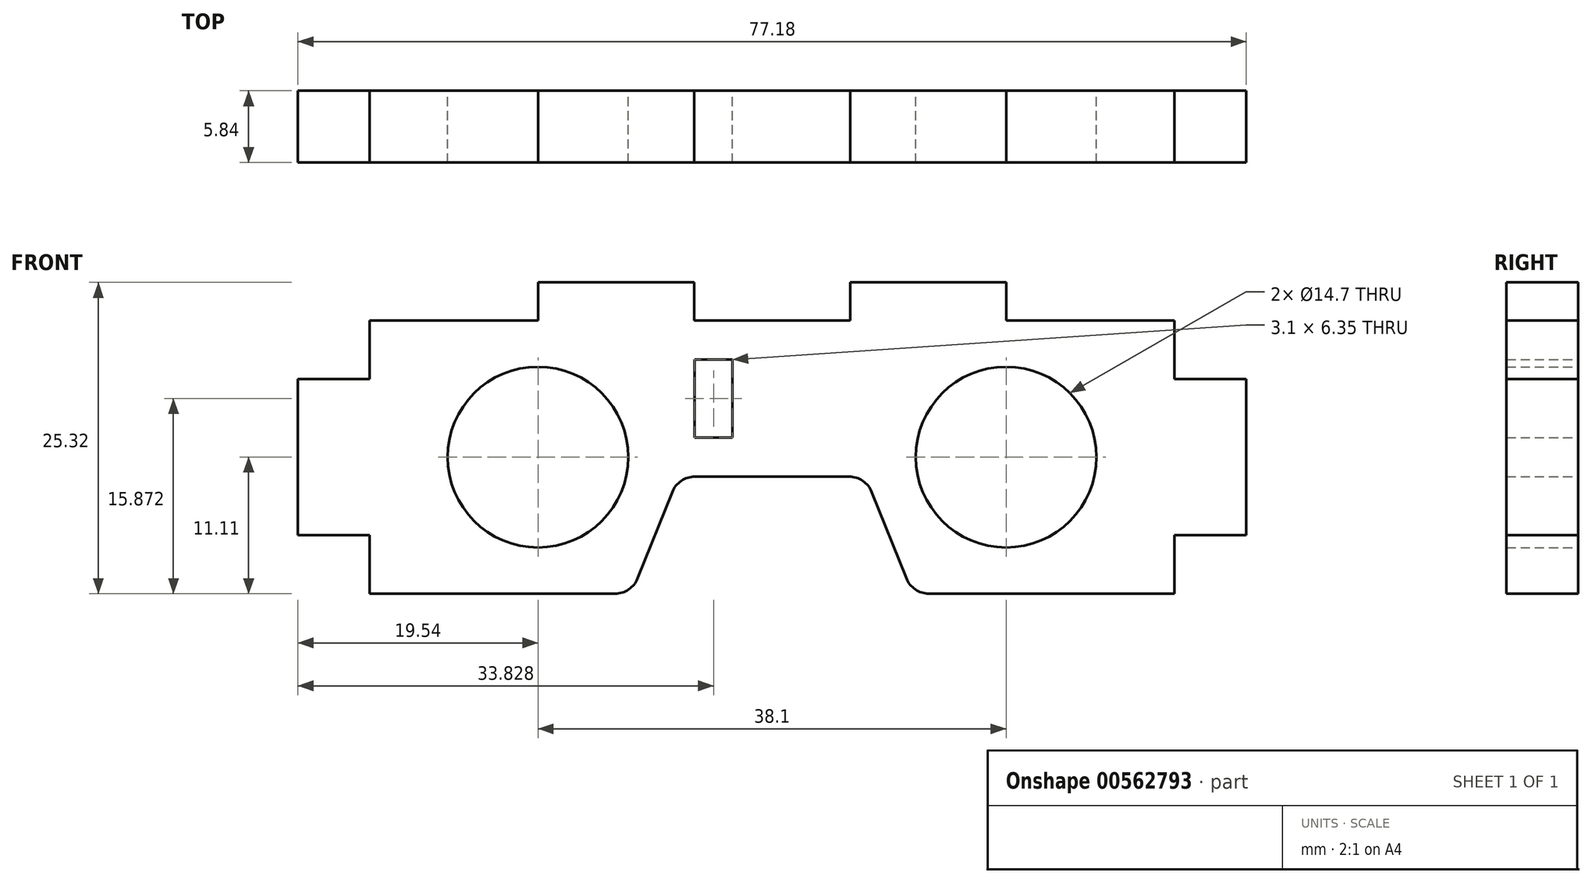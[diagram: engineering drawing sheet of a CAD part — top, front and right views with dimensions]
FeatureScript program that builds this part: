
annotation { "Feature Type Name" : "Feature", "Feature Type Description" : "" }
export const myFeature = defineFeature(function(context is Context, id is Id, definition is map)
    precondition{}
    {
        {
            var Q0;
            Q0=qCreatedBy(makeId("Front.planeOp"),FACE);
            var sketch = newSketch(context, id + "F0", { "sketchPlane" : qUnion([Q0])});
            skCircle(sketch, "E0", {"center": v(-19.05, 0) * mm, "radius": 7.35 * mm});
            skCircle(sketch, "E1.MirrorC", {"center": v(19.05, 0) * mm, "radius": 7.35 * mm});
            skLineSegment(sketch, "E2.bottom", {"start": v(-31.75, 11.11) * mm, "end": v(31.75, 11.11) * mm});
            skLineSegment(sketch, "E2.top", {"start": v(-31.75, -11.11) * mm, "end": v(-11.43, -11.11) * mm});
            skLineSegment(sketch, "E2.left", {"start": v(-31.75, 11.11) * mm, "end": v(-31.75, -11.11) * mm});
            skLineSegment(sketch, "E2.right", {"start": v(31.75, 11.11) * mm, "end": v(31.75, -11.11) * mm});
            skPoint(sketch, "E2.middle", {"position": v(0, 0) * mm});
            skLineSegment(sketch, "E3", {"start": v(-11.43, -11.11) * mm, "end": v(-7.62, -1.59) * mm});
            skLineSegment(sketch, "E4", {"start": v(-7.62, -1.59) * mm, "end": v(0, -1.59) * mm});
            skLineSegment(sketch, "E5.MirrorCS", {"start": v(7.62, -1.59) * mm, "end": v(0, -1.59) * mm});
            skLineSegment(sketch, "E6.MirrorCS", {"start": v(11.43, -11.11) * mm, "end": v(7.62, -1.59) * mm});
            skLineSegment(sketch, "E7.trimOffspring", {"start": v(11.43, -11.11) * mm, "end": v(31.75, -11.11) * mm});
            skSolve(sketch);
        }
        {
            var Q0;
            Q0=makeQuery(id+"F0.imprint","IMPRINT",FACE,{"disambiguationData":[TD([[makeQuery(id+"F0.imprint","IMPRINT",EDGE,{"derivedFrom":sQuery(id+"F0.wireOp",EDGE,"E0")}),-1.0]])]});
            extrude(context, id + "F1", {"entities" : qUnion([Q0]), "depth" : 5.84 * mm, "offsetDistance" : 25.4 * mm});
        }
        {
            var Q0;
            Q0=makeQuery(id+"F1.opExtrude","SWEPT_EDGE",EDGE,{"disambiguationData":[OSD([sQuery(id+"F0.wireOp",EDGE,"E2.top"),sQuery(id+"F0.wireOp",EDGE,"E3")])]});
            var Q1;
            Q1=makeQuery(id+"F1.opExtrude","SWEPT_EDGE",EDGE,{"disambiguationData":[OSD([sQuery(id+"F0.wireOp",EDGE,"E3"),sQuery(id+"F0.wireOp",EDGE,"E4")])]});
            var Q2;
            Q2=makeQuery(id+"F1.opExtrude","SWEPT_EDGE",EDGE,{"disambiguationData":[OSD([sQuery(id+"F0.wireOp",EDGE,"E5.MirrorCS"),sQuery(id+"F0.wireOp",EDGE,"E6.MirrorCS")])]});
            var Q3;
            Q3=makeQuery(id+"F1.opExtrude","SWEPT_EDGE",EDGE,{"disambiguationData":[OSD([sQuery(id+"F0.wireOp",EDGE,"E6.MirrorCS"),sQuery(id+"F0.wireOp",EDGE,"E7.trimOffspring")])]});
            fillet(context, id + "F2", {"entities" : qUnion([Q0, Q1, Q2, Q3]), "radius" : 2 * mm, "tangentPropagation" : true, "allowEdgeOverflow" : false});
        }
        {
            var Q0;
            Q0=makeQuery(id+"F1.opExtrude","CAP_FACE",FACE,{"disambiguationData":[OSD([sQuery(id+"F0.wireOp",EDGE,"E0"),sQuery(id+"F0.wireOp",EDGE,"E1.MirrorC"),sQuery(id+"F0.wireOp",EDGE,"E2.bottom"),sQuery(id+"F0.wireOp",EDGE,"E2.top"),sQuery(id+"F0.wireOp",EDGE,"E2.left"),sQuery(id+"F0.wireOp",EDGE,"E2.right"),sQuery(id+"F0.wireOp",EDGE,"E3"),sQuery(id+"F0.wireOp",EDGE,"E4"),sQuery(id+"F0.wireOp",EDGE,"E5.MirrorCS"),sQuery(id+"F0.wireOp",EDGE,"E6.MirrorCS"),sQuery(id+"F0.wireOp",EDGE,"E7.trimOffspring")])],"isStart":true});
            var sketch = newSketch(context, id + "F3", { "sketchPlane" : qUnion([Q0])});
            skLineSegment(sketch, "E8.bottom", {"start": v(6.31, 1.59) * mm, "end": v(3.21, 1.59) * mm});
            skLineSegment(sketch, "E8.top", {"start": v(6.31, 7.94) * mm, "end": v(3.21, 7.94) * mm});
            skLineSegment(sketch, "E8.left", {"start": v(6.31, 1.59) * mm, "end": v(6.31, 7.94) * mm});
            skLineSegment(sketch, "E8.right", {"start": v(3.21, 1.59) * mm, "end": v(3.21, 7.94) * mm});
            skPoint(sketch, "E8.middle", {"position": v(4.76, 4.76) * mm});
            skSolve(sketch);
        }
        {
            var Q0;
            Q0 = qSketchRegion(id + "F3", true);
            extrude(context, id + "F4", {"entities" : qUnion([Q0]), "operationType" : NewBodyOperationType.REMOVE, "oppositeDirection" : true, "depth" : 25.4 * mm, "offsetDistance" : 25.4 * mm});
        }
        {
            var Q0;
            Q0=makeQuery(id+"F1.opExtrude","CAP_FACE",FACE,{"disambiguationData":[OSD([sQuery(id+"F0.wireOp",EDGE,"E0"),sQuery(id+"F0.wireOp",EDGE,"E1.MirrorC"),sQuery(id+"F0.wireOp",EDGE,"E2.bottom"),sQuery(id+"F0.wireOp",EDGE,"E2.top"),sQuery(id+"F0.wireOp",EDGE,"E2.left"),sQuery(id+"F0.wireOp",EDGE,"E2.right"),sQuery(id+"F0.wireOp",EDGE,"E3"),sQuery(id+"F0.wireOp",EDGE,"E4"),sQuery(id+"F0.wireOp",EDGE,"E5.MirrorCS"),sQuery(id+"F0.wireOp",EDGE,"E6.MirrorCS"),sQuery(id+"F0.wireOp",EDGE,"E7.trimOffspring")])],"isStart":false});
            var sketch = newSketch(context, id + "F5", { "sketchPlane" : qUnion([Q0])});
            skLineSegment(sketch, "E9.bottom", {"start": v(-19.05, 11.11) * mm, "end": v(-6.35, 11.11) * mm});
            skLineSegment(sketch, "E9.top", {"start": v(-19.05, 14.21) * mm, "end": v(-6.35, 14.21) * mm});
            skLineSegment(sketch, "E9.left", {"start": v(-19.05, 11.11) * mm, "end": v(-19.05, 14.21) * mm});
            skLineSegment(sketch, "E9.right", {"start": v(-6.35, 11.11) * mm, "end": v(-6.35, 14.21) * mm});
            skPoint(sketch, "E9.middle", {"position": v(-12.7, 12.66) * mm});
            skLineSegment(sketch, "E10.MirrorCS", {"start": v(19.05, 11.11) * mm, "end": v(19.05, 14.21) * mm});
            skLineSegment(sketch, "E11.MirrorCS", {"start": v(19.05, 14.21) * mm, "end": v(6.35, 14.21) * mm});
            skLineSegment(sketch, "E12.MirrorCS", {"start": v(19.05, 11.11) * mm, "end": v(6.35, 11.11) * mm});
            skPoint(sketch, "E13.MirrorP", {"position": v(12.7, 12.66) * mm});
            skLineSegment(sketch, "E14.MirrorCS", {"start": v(6.35, 11.11) * mm, "end": v(6.35, 14.21) * mm});
            skSolve(sketch);
        }
        {
            var Q0;
            Q0 = qSketchRegion(id + "F5", true);
            var Q1;
            Q1=makeQuery(id+"F1.opExtrude","CAP_FACE",FACE,{"disambiguationData":[OSD([sQuery(id+"F0.wireOp",EDGE,"E0"),sQuery(id+"F0.wireOp",EDGE,"E1.MirrorC"),sQuery(id+"F0.wireOp",EDGE,"E2.bottom"),sQuery(id+"F0.wireOp",EDGE,"E2.top"),sQuery(id+"F0.wireOp",EDGE,"E2.left"),sQuery(id+"F0.wireOp",EDGE,"E2.right"),sQuery(id+"F0.wireOp",EDGE,"E3"),sQuery(id+"F0.wireOp",EDGE,"E4"),sQuery(id+"F0.wireOp",EDGE,"E5.MirrorCS"),sQuery(id+"F0.wireOp",EDGE,"E6.MirrorCS"),sQuery(id+"F0.wireOp",EDGE,"E7.trimOffspring")])],"isStart":true});
            extrude(context, id + "F6", {"entities" : qUnion([Q0]), "operationType" : NewBodyOperationType.ADD, "endBound" : BoundingType.UP_TO_SURFACE, "oppositeDirection" : true, "depth" : 25.4 * mm, "endBoundEntityFace" : qUnion([Q1]), "offsetDistance" : 25.4 * mm});
        }
        {
            var Q0;
            Q0=makeQuery(id+"F6.boolean.opBoolean","MERGE",FACE,{"derivedFrom":[makeQuery(id+"F1.opExtrude","CAP_FACE",FACE,{"disambiguationData":[OSD([sQuery(id+"F0.wireOp",EDGE,"E0"),sQuery(id+"F0.wireOp",EDGE,"E1.MirrorC"),sQuery(id+"F0.wireOp",EDGE,"E2.bottom"),sQuery(id+"F0.wireOp",EDGE,"E2.top"),sQuery(id+"F0.wireOp",EDGE,"E2.left"),sQuery(id+"F0.wireOp",EDGE,"E2.right"),sQuery(id+"F0.wireOp",EDGE,"E3"),sQuery(id+"F0.wireOp",EDGE,"E4"),sQuery(id+"F0.wireOp",EDGE,"E5.MirrorCS"),sQuery(id+"F0.wireOp",EDGE,"E6.MirrorCS"),sQuery(id+"F0.wireOp",EDGE,"E7.trimOffspring")])],"isStart":false}),makeQuery(id+"F6.opExtrude","CAP_FACE",FACE,{"disambiguationData":[OSD([sQuery(id+"F5.wireOp",EDGE,"E9.bottom"),sQuery(id+"F5.wireOp",EDGE,"E9.top"),sQuery(id+"F5.wireOp",EDGE,"E9.left"),sQuery(id+"F5.wireOp",EDGE,"E9.right")])],"isStart":true}),makeQuery(id+"F6.opExtrude","CAP_FACE",FACE,{"disambiguationData":[OSD([sQuery(id+"F5.wireOp",EDGE,"E10.MirrorCS"),sQuery(id+"F5.wireOp",EDGE,"E11.MirrorCS"),sQuery(id+"F5.wireOp",EDGE,"E12.MirrorCS"),sQuery(id+"F5.wireOp",EDGE,"E14.MirrorCS")])],"isStart":true})]});
            var sketch = newSketch(context, id + "F7", { "sketchPlane" : qUnion([Q0])});
            skLineSegment(sketch, "E15.bottom", {"start": v(32.75, 6.35) * mm, "end": v(38.6, 6.35) * mm});
            skLineSegment(sketch, "E15.top", {"start": v(32.75, -6.35) * mm, "end": v(38.6, -6.35) * mm});
            skLineSegment(sketch, "E15.left", {"start": v(31.75, 6.35) * mm, "end": v(31.75, -6.35) * mm});
            skLineSegment(sketch, "E15.right", {"start": v(38.6, 6.35) * mm, "end": v(38.6, -6.35) * mm});
            skPoint(sketch, "E15.middle", {"position": v(35.17, 0) * mm});
            skPoint(sketch, "E16.MirrorP", {"position": v(-35.17, 0) * mm});
            skLineSegment(sketch, "E17.bottom", {"start": v(31.75, 11.11) * mm, "end": v(32.75, 11.11) * mm});
            skLineSegment(sketch, "E17.top", {"start": v(31.75, -11.11) * mm, "end": v(32.75, -11.11) * mm});
            skLineSegment(sketch, "E17.left", {"start": v(31.75, 11.11) * mm, "end": v(31.75, -11.11) * mm});
            skLineSegment(sketch, "E17.right", {"start": v(32.75, 11.11) * mm, "end": v(32.75, 6.35) * mm});
            skLineSegment(sketch, "E18.trimOffspring", {"start": v(32.75, -6.35) * mm, "end": v(32.75, -11.11) * mm});
            skPoint(sketch, "E19.MirrorCS.start.orphan", {"position": v(-38.6, 6.35) * mm});
            skPoint(sketch, "E20.MirrorCS.start.orphan", {"position": v(-31.75, 6.35) * mm});
            skPoint(sketch, "E21.MirrorCS.end.orphan", {"position": v(-38.6, -6.35) * mm});
            skPoint(sketch, "E21.MirrorCS.start.orphan", {"position": v(-31.75, -6.35) * mm});
            skLineSegment(sketch, "E22.MirrorCS", {"start": v(-31.75, 11.11) * mm, "end": v(-32.75, 11.11) * mm});
            skLineSegment(sketch, "E23.MirrorCS", {"start": v(-31.75, -11.11) * mm, "end": v(-32.75, -11.11) * mm});
            skLineSegment(sketch, "E24.MirrorCS", {"start": v(-31.75, 6.35) * mm, "end": v(-31.75, -6.35) * mm});
            skLineSegment(sketch, "E25.MirrorCS", {"start": v(-32.75, -6.35) * mm, "end": v(-32.75, -11.11) * mm});
            skLineSegment(sketch, "E26.MirrorCS", {"start": v(-32.75, 11.11) * mm, "end": v(-32.75, 6.35) * mm});
            skLineSegment(sketch, "E27.MirrorCS", {"start": v(-32.75, -6.35) * mm, "end": v(-38.6, -6.35) * mm});
            skLineSegment(sketch, "E28.MirrorCS", {"start": v(-32.75, 6.35) * mm, "end": v(-38.6, 6.35) * mm});
            skLineSegment(sketch, "E29.MirrorCS", {"start": v(-38.6, 6.35) * mm, "end": v(-38.6, -6.35) * mm});
            skLineSegment(sketch, "E30.MirrorCS", {"start": v(-31.75, 11.11) * mm, "end": v(-31.75, -11.11) * mm});
            skSolve(sketch);
        }
        {
            var Q0;
            Q0 = qSketchRegion(id + "F7", true);
            var Q1;
            {var subQ0=sQuery(id+"F0.wireOp",EDGE,"E7.trimOffspring");var subQ1=sQuery(id+"F0.wireOp",EDGE,"E6.MirrorCS");var subQ2=sQuery(id+"F0.wireOp",EDGE,"E5.MirrorCS");var subQ3=sQuery(id+"F0.wireOp",EDGE,"E4");var subQ4=sQuery(id+"F0.wireOp",EDGE,"E3");var subQ5=sQuery(id+"F0.wireOp",EDGE,"E2.right");var subQ6=sQuery(id+"F0.wireOp",EDGE,"E2.left");var subQ7=sQuery(id+"F0.wireOp",EDGE,"E2.top");var subQ8=sQuery(id+"F0.wireOp",EDGE,"E2.bottom");var subQ9=sQuery(id+"F0.wireOp",EDGE,"E1.MirrorC");var subQ10=sQuery(id+"F0.wireOp",EDGE,"E0");Q1=makeQuery(id+"F6.boolean.opBoolean","MERGE",FACE,{"derivedFrom":[makeQuery(id+"F1.opExtrude","CAP_FACE",FACE,{"disambiguationData":[OSD([subQ10,subQ9,subQ8,subQ7,subQ6,subQ5,subQ4,subQ3,subQ2,subQ1,subQ0])],"isStart":true}),makeQuery(id+"F6.opExtrude","CAP_FACE",FACE,{"disambiguationData":[OSD([subQ10,subQ9,subQ8,subQ7,subQ6,subQ5,subQ4,subQ3,subQ2,subQ1,subQ0]),OD(0.0)],"isStart":false}),makeQuery(id+"F6.opExtrude","CAP_FACE",FACE,{"disambiguationData":[OSD([subQ10,subQ9,subQ8,subQ7,subQ6,subQ5,subQ4,subQ3,subQ2,subQ1,subQ0]),OD(1.0)],"isStart":false})]});}
            extrude(context, id + "F8", {"entities" : qUnion([Q0]), "operationType" : NewBodyOperationType.ADD, "endBound" : BoundingType.UP_TO_SURFACE, "oppositeDirection" : true, "depth" : 25.4 * mm, "endBoundEntityFace" : qUnion([Q1]), "offsetDistance" : 25.4 * mm});
        }
    });
